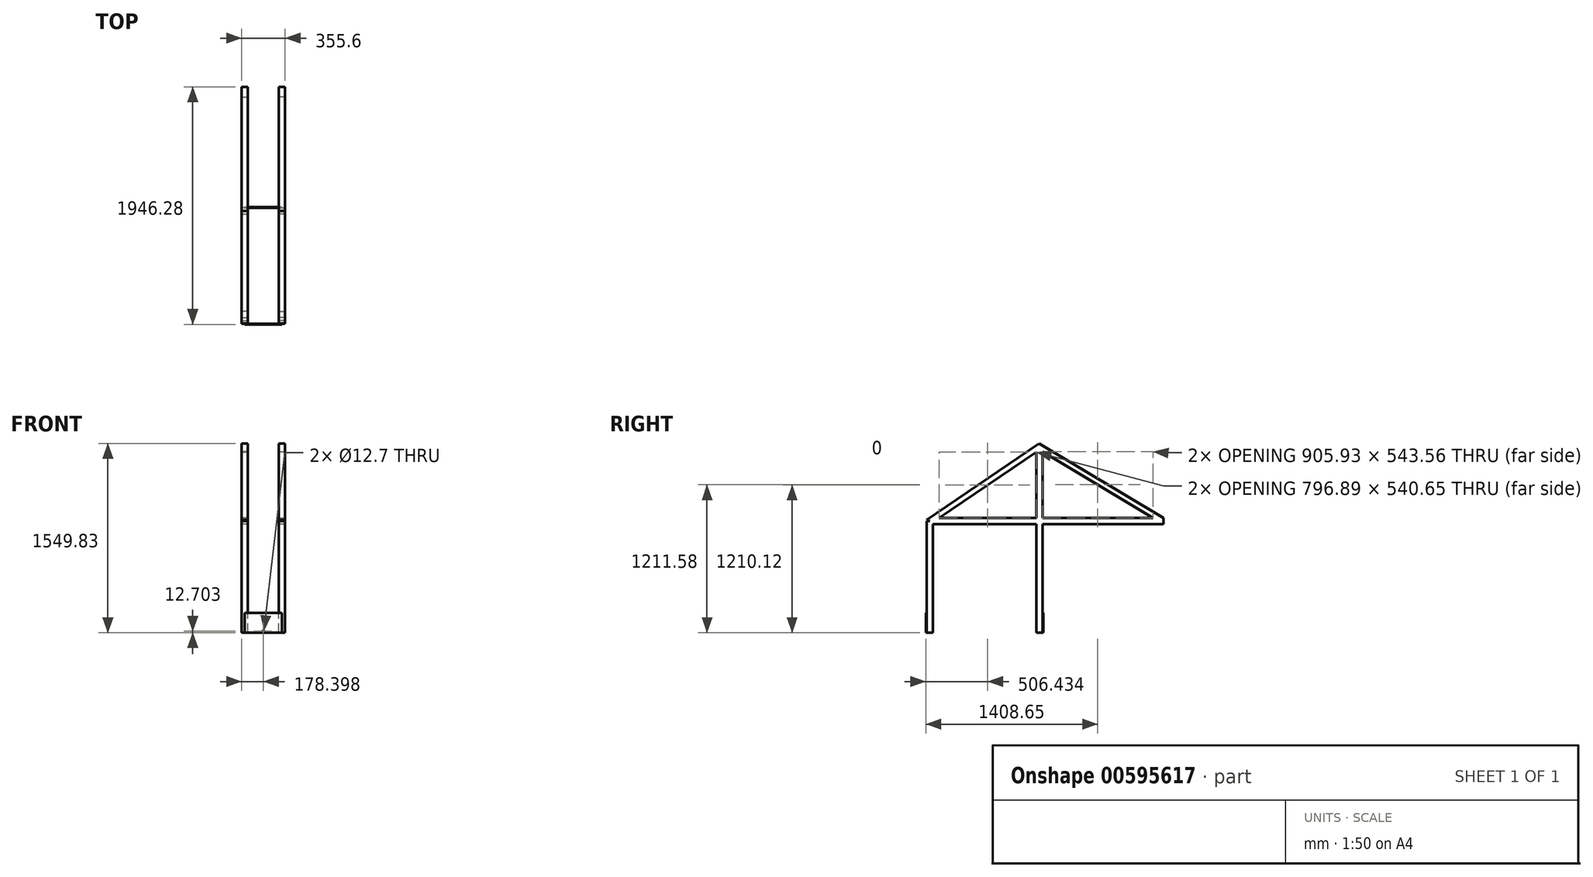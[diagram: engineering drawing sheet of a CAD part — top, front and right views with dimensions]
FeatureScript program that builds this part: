
annotation { "Feature Type Name" : "Feature", "Feature Type Description" : "" }
export const myFeature = defineFeature(function(context is Context, id is Id, definition is map)
    precondition{}
    {
        {
            var Q0;
            Q0=qCreatedBy(makeId("Right.planeOp"),FACE);
            var sketch = newSketch(context, id + "F0", { "sketchPlane" : qUnion([Q0])});
            skLineSegment(sketch, "E0", {"start": v(-898.52, 0) * mm, "end": v(-898.52, 914.4) * mm});
            skLineSegment(sketch, "E1", {"start": v(-898.52, 914.4) * mm, "end": v(0, 914.4) * mm});
            skLineSegment(sketch, "E2", {"start": v(0, 914.4) * mm, "end": v(0, 0) * mm});
            skLineSegment(sketch, "E3", {"start": v(0, 914.4) * mm, "end": v(1016, 914.4) * mm});
            skLineSegment(sketch, "E4", {"start": v(1016, 914.4) * mm, "end": v(0, 1524) * mm});
            skLineSegment(sketch, "E5", {"start": v(0, 1524) * mm, "end": v(0, 914.4) * mm});
            skLineSegment(sketch, "E6", {"start": v(0, 1524) * mm, "end": v(-898.52, 914.4) * mm});
            skSolve(sketch);
        }
        {
            var Q0;
            Q0=qCreatedBy(makeId("Top.planeOp"),FACE);
            var sketch = newSketch(context, id + "F1", { "sketchPlane" : qUnion([Q0])});
            skLineSegment(sketch, "E7", {"start": v(0, 0) * mm, "end": v(74.53, 0) * mm, "construction": true});
            skLineSegment(sketch, "E8", {"start": v(0, 0) * mm, "end": v(0, -78.2) * mm, "construction": true});
            skLineSegment(sketch, "E9.bottom", {"start": v(25.4, -25.4) * mm, "end": v(-25.4, -25.4) * mm});
            skLineSegment(sketch, "E9.top", {"start": v(25.4, 25.4) * mm, "end": v(-25.4, 25.4) * mm});
            skLineSegment(sketch, "E9.left", {"start": v(25.4, -25.4) * mm, "end": v(25.4, 25.4) * mm});
            skLineSegment(sketch, "E9.right", {"start": v(-25.4, -25.4) * mm, "end": v(-25.4, 25.4) * mm});
            skSolve(sketch);
        }
        {
            var Q0;
            Q0=makeQuery(id+"F1.imprint","IMPRINT",FACE,{"disambiguationData":[TD([[makeQuery(id+"F1.imprint","IMPRINT",EDGE,{"derivedFrom":sQuery(id+"F1.wireOp",EDGE,"E9.bottom")}),-1.0]])]});
            var Q1;
            Q1=sQuery(id+"F0.wireOp",EDGE,"E2");
            var Q2;
            Q2=sQuery(id+"F0.wireOp",EDGE,"E5");
            sweep(context, id + "F2", {"profiles" : qUnion([Q0]), "path" : qUnion([Q1, Q2])});
        }
        {
            var Q0;
            Q0=sQuery(id+"F0.wireOp",VERTEX,"E3.end");
            var Q1;
            Q1=qCreatedBy(makeId("Front.planeOp"),FACE);
            cPlane(context, id + "F3", {"entities" : qUnion([Q0, Q1]), "cplaneType" : CPlaneType.PLANE_POINT, "offset" : 25.4 * mm, "width" : 152.4 * mm, "height" : 152.4 * mm});
        }
        {
            var Q0;
            Q0=qCreatedBy(id+"F3.planeOp",FACE);
            var sketch = newSketch(context, id + "F4", { "sketchPlane" : qUnion([Q0])});
            skLineSegment(sketch, "E10.bottom", {"start": v(25.4, 939.8) * mm, "end": v(-25.4, 939.8) * mm});
            skLineSegment(sketch, "E10.top", {"start": v(25.4, 889) * mm, "end": v(-25.4, 889) * mm});
            skLineSegment(sketch, "E10.left", {"start": v(25.4, 939.8) * mm, "end": v(25.4, 889) * mm});
            skLineSegment(sketch, "E10.right", {"start": v(-25.4, 939.8) * mm, "end": v(-25.4, 889) * mm});
            skLineSegment(sketch, "E11", {"start": v(0, 914.4) * mm, "end": v(-179.96, 914.4) * mm, "construction": true});
            skLineSegment(sketch, "E12", {"start": v(0, 914.4) * mm, "end": v(0, 693.47) * mm, "construction": true});
            skSolve(sketch);
        }
        {
            var Q0;
            Q0=makeQuery(id+"F4.imprint","IMPRINT",FACE,{"disambiguationData":[TD([[makeQuery(id+"F4.imprint","IMPRINT",EDGE,{"derivedFrom":sQuery(id+"F4.wireOp",EDGE,"E10.bottom")}),1.0]])]});
            var Q1;
            Q1=sQuery(id+"F0.wireOp",EDGE,"E3");
            var Q2;
            Q2=sQuery(id+"F0.wireOp",EDGE,"E1");
            sweep(context, id + "F5", {"operationType" : NewBodyOperationType.ADD, "profiles" : qUnion([Q0]), "path" : qUnion([Q1, Q2])});
        }
        {
            var Q0;
            Q0 = qSketchRegion(id + "F4", true);
            var Q1;
            Q1=sQuery(id+"F0.wireOp",EDGE,"E4");
            var Q2;
            Q2=sQuery(id+"F0.wireOp",EDGE,"E6");
            sweep(context, id + "F6", {"operationType" : NewBodyOperationType.ADD, "profiles" : qUnion([Q0]), "path" : qUnion([Q1, Q2])});
        }
        {
            var Q0;
            Q0=qCreatedBy(makeId("Top.planeOp"),FACE);
            var sketch = newSketch(context, id + "F7", { "sketchPlane" : qUnion([Q0])});
            skLineSegment(sketch, "E13.bottom", {"start": v(-25.4, -923.93) * mm, "end": v(25.4, -923.93) * mm});
            skLineSegment(sketch, "E13.top", {"start": v(-25.4, -873.13) * mm, "end": v(25.4, -873.13) * mm});
            skLineSegment(sketch, "E13.left", {"start": v(-25.4, -923.93) * mm, "end": v(-25.4, -873.12) * mm});
            skLineSegment(sketch, "E13.right", {"start": v(25.4, -923.93) * mm, "end": v(25.4, -873.12) * mm});
            skLineSegment(sketch, "E14", {"start": v(0, -898.52) * mm, "end": v(120.24, -898.52) * mm, "construction": true});
            skSolve(sketch);
        }
        {
            var Q0;
            Q0=makeQuery(id+"F7.imprint","IMPRINT",FACE,{"disambiguationData":[TD([[makeQuery(id+"F7.imprint","IMPRINT",EDGE,{"derivedFrom":sQuery(id+"F7.wireOp",EDGE,"E13.bottom")}),1.0]])]});
            var Q1;
            Q1=sQuery(id+"F0.wireOp",EDGE,"E0");
            sweep(context, id + "F8", {"operationType" : NewBodyOperationType.ADD, "profiles" : qUnion([Q0]), "path" : qUnion([Q1])});
        }
        {
            var Q0;
            Q0=qCreatedBy(makeId("Right.planeOp"),FACE);
            cPlane(context, id + "F9", {"entities" : qUnion([Q0]), "cplaneType" : CPlaneType.OFFSET, "offset" : 152.4 * mm, "width" : 152.4 * mm, "height" : 152.4 * mm});
        }
        {
            var Q0;
            Q0=makeQuery(id+"F2.opSweep","SWEPT_BODY",BODY,{"disambiguationData":[OSD([sQuery(id+"F0.wireOp",EDGE,"E5"),sQuery(id+"F1.wireOp",EDGE,"E9.bottom"),sQuery(id+"F1.wireOp",EDGE,"E9.top"),sQuery(id+"F1.wireOp",EDGE,"E9.left"),sQuery(id+"F1.wireOp",EDGE,"E9.right")])]});
            var Q1;
            Q1=qCreatedBy(id+"F9.planeOp",FACE);
            mirror(context, id + "F10", {"entities" : qUnion([Q0]), "mirrorPlane" : qUnion([Q1])});
        }
        {
            var Q0;
            Q0=makeQuery(id+"F10.opPattern","COPY",FACE,{"derivedFrom":makeQuery(id+"F8.opSweep","SWEPT_FACE",FACE,{"disambiguationData":[OSD([sQuery(id+"F0.wireOp",EDGE,"E0"),sQuery(id+"F7.wireOp",EDGE,"E13.bottom")])]}),"instanceName":"1"});
            var sketch = newSketch(context, id + "F11", { "sketchPlane" : qUnion([Q0])});
            skLineSegment(sketch, "E15.bottom", {"start": v(0, 162.56) * mm, "end": v(304.8, 162.56) * mm});
            skLineSegment(sketch, "E15.top", {"start": v(0, 0) * mm, "end": v(304.8, 0) * mm});
            skLineSegment(sketch, "E15.left", {"start": v(0, 162.56) * mm, "end": v(0, 0) * mm});
            skLineSegment(sketch, "E15.right", {"start": v(304.8, 162.56) * mm, "end": v(304.8, 0) * mm});
            skSolve(sketch);
        }
        {
            var Q0;
            {var subQ0=sQuery(id+"F11.wireOp",EDGE,"E15.left");Q0=makeQuery(id+"F11.imprint","IMPRINT",FACE,{"disambiguationData":[TD([[makeQuery(id+"F11.imprint","IMPRINT",EDGE,{"derivedFrom":subQ0}),1.0]])]});}
            var Q1;
            {var subQ0=sQuery(id+"F11.wireOp",EDGE,"E15.right");Q1=makeQuery(id+"F11.imprint","IMPRINT",FACE,{"disambiguationData":[TD([[makeQuery(id+"F11.imprint","IMPRINT",EDGE,{"derivedFrom":subQ0}),-1.0]])]});}
            extrude(context, id + "F12", {"entities" : qUnion([Q0, Q1]), "depth" : 6.35 * mm, "offsetDistance" : 25.4 * mm});
        }
        {
            var Q0;
            {var subQ0=sQuery(id+"F0.wireOp",EDGE,"E3");var subQ2=sQuery(id+"F0.wireOp",EDGE,"E2");var subQ4=sQuery(id+"F1.wireOp",EDGE,"E9.top");Q0=makeQuery(id+"F10.opPattern","COPY",FACE,{"derivedFrom":makeQuery(id+"F5.boolean.opBoolean","SPLIT",FACE,{"disambiguationData":[TD([makeQuery(id+"F5.opSweep","SWEPT_FACE",FACE,{"disambiguationData":[OSD([subQ0,sQuery(id+"F4.wireOp",EDGE,"E10.top")])]})])],"derivedFrom":makeQuery(id+"F2.opSweep","SWEPT_FACE",FACE,{"disambiguationData":[OSD([subQ2,subQ4])]})}),"instanceName":"1"});}
            var sketch = newSketch(context, id + "F13", { "sketchPlane" : qUnion([Q0])});
            skLineSegment(sketch, "E16.0.0", {"start": v(0, 0) * mm, "end": v(0, 162.56) * mm});
            skLineSegment(sketch, "E16.0.1", {"start": v(0, 162.56) * mm, "end": v(-304.8, 162.56) * mm});
            skLineSegment(sketch, "E16.0.2", {"start": v(-304.8, 162.56) * mm, "end": v(-304.8, 0) * mm});
            skLineSegment(sketch, "E16.0.3", {"start": v(-304.8, 0) * mm, "end": v(0, 0) * mm});
            skSolve(sketch);
        }
        {
            var Q0;
            Q0 = qSketchRegion(id + "F13", true);
            extrude(context, id + "F14", {"entities" : qUnion([Q0]), "depth" : 6.35 * mm, "offsetDistance" : 25.4 * mm});
        }
        {
            var Q0;
            Q0=qCreatedBy(makeId("Top.planeOp"),FACE);
            cPlane(context, id + "F15", {"entities" : qUnion([Q0]), "cplaneType" : CPlaneType.OFFSET, "offset" : 82.55 * mm, "width" : 152.4 * mm, "height" : 152.4 * mm});
        }
        {
            var Q0;
            Q0=qCreatedBy(id+"F15.planeOp",FACE);
            var sketch = newSketch(context, id + "F16", { "sketchPlane" : qUnion([Q0])});
            skLineSegment(sketch, "E17", {"start": v(152.4, 36.2) * mm, "end": v(152.4, -1137.1) * mm, "construction": true});
            skSolve(sketch);
        }
        {
            var Q0;
            Q0=qCreatedBy(makeId("Front.planeOp"),FACE);
            var sketch = newSketch(context, id + "F17", { "sketchPlane" : qUnion([Q0])});
            skCircle(sketch, "E18", {"center": v(152.4, 82.55) * mm, "radius": 69.85 * mm});
            skCircle(sketch, "E19", {"center": v(153, 12.7) * mm, "radius": 6.35 * mm});
            skSolve(sketch);
        }
        {
            var Q0;
            Q0=makeQuery(id+"F17.imprint","IMPRINT",FACE,{"disambiguationData":[TD([[makeQuery(id+"F17.imprint","IMPRINT",EDGE,{"derivedFrom":sQuery(id+"F17.wireOp",EDGE,"E19")}),1.0]])]});
            var Q1;
            Q1=sQuery(id+"F17.wireOp",EDGE,"E19");
            extrude(context, id + "F18", {"entities" : qUnion([Q0]), "operationType" : NewBodyOperationType.REMOVE, "surfaceEntities" : qUnion([Q1]), "endBound" : BoundingType.THROUGH_ALL, "depth" : 25.4 * mm, "offsetDistance" : 25.4 * mm, "hasSecondDirection" : true, "secondDirectionBound" : SecondDirectionBoundingType.THROUGH_ALL, "secondDirectionOppositeDirection" : true, "secondDirectionDepth" : 25.4 * mm});
        }
    });
